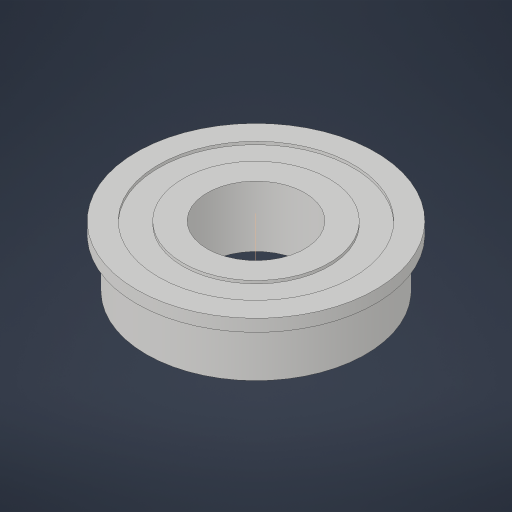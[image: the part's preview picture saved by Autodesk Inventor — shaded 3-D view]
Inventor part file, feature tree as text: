
AUTODESK INVENTOR PART (.ipt)
format: ipt  version: 2023.4 (Build 274418000, 418)  size: 185,344 bytes
history: native  units: in
note: dims shown in document units (in); Inventor stores cm internally (conversion verified against a paired STEP export)
features: revolve x1
ambient origin geometry x8: Origin, YZ Plane, XZ Plane, XY Plane, X Axis, Y Axis, Z Axis, Center Point
bodies: Solid1 (feature_tree)
feature tree (1):
  revolve  "Revolve1"  [1 undecoded]
note: 1 required parameter value undecoded (feature->parameter linkage not recoverable at this tier; creation-order binding heuristic only, values carry confidence <= 0.55)
